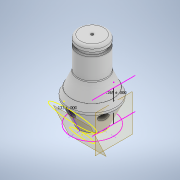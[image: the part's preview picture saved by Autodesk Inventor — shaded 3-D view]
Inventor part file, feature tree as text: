
AUTODESK INVENTOR PART (.ipt)
format: ipt  version: 2020 (Build 240168000, 168)  size: 301,568 bytes
history: native  units: in
note: dims shown in document units (in); Inventor stores cm internally (conversion verified against a paired STEP export)
features: sketch x6, hole x4, plane x2, fillet x2, revolve x1, pattern_circular x1
ambient origin geometry x8: Origin, YZ Plane, XZ Plane, XY Plane, X Axis, Y Axis, Z Axis, Center Point
bodies: Solid1 (feature_tree)
feature tree (16):
  revolve  "Revolution1"  [1 undecoded]
  hole  "Hole4"  [1 undecoded]
  hole  "Hole8"  [1 undecoded]
  sketch  "Sketch13"  dims[d2=90.0deg d3=0.057in]
  plane  "Work Plane6"
  sketch  "Sketch14"  dims[d4=0.095in d5=0.125in]
  sketch  "Sketch29"  dims[d24=0.4466in d25=0.125in]
  plane  "Work Plane5"
  sketch  "Sketch30"  dims[d54=0.3779in d72=0.3779in d83=0.75in d84=0.75in d85=0.0625in d86=0.75in d87=0.375in d88=0.25in d89=0.5635in d90=1.1in d91=0.8108in d92=0.2645in d121=0.196in d122=0.25in d123=0.375in d124=0.25in d125=0.5635in d126=0.25in d127=0.0in d137=0.3779in d155=0.3779in d173=0.3779in d191=0.3779in d221=0.3779in d239=0.3779in d253=0.4466in d254=0.1325in d255=0.0625in d256=0.25in d257=0.375in d258=0.25in d259=0.5635in d260=0.55in d261=0.0in d262=0.213in d263=0.25in d264=0.375in d265=0.25in d266=0.5635in d267=0.25in d268=0.0in d269=1.5748in d270=1.3743in d272=0.0625in d273=0.0625in]
  hole  "Hole9"  [1 undecoded]
  hole  "Hole10"  [1 undecoded]
  pattern_circular  "Circular Pattern7"  [2 undecoded]
  fillet  "Fillet1"  Radius=0.75in
  fillet  "Fillet2"  Radius=0.75in
  sketch  "Sketch12"  dims[d0=0.3328in d1=0.5in]
  sketch  "Sketch16"  dims[d6=90.0deg d23=0.65in]
note: 7 required parameter values undecoded (feature->parameter linkage not recoverable at this tier; creation-order binding heuristic only, values carry confidence <= 0.55)